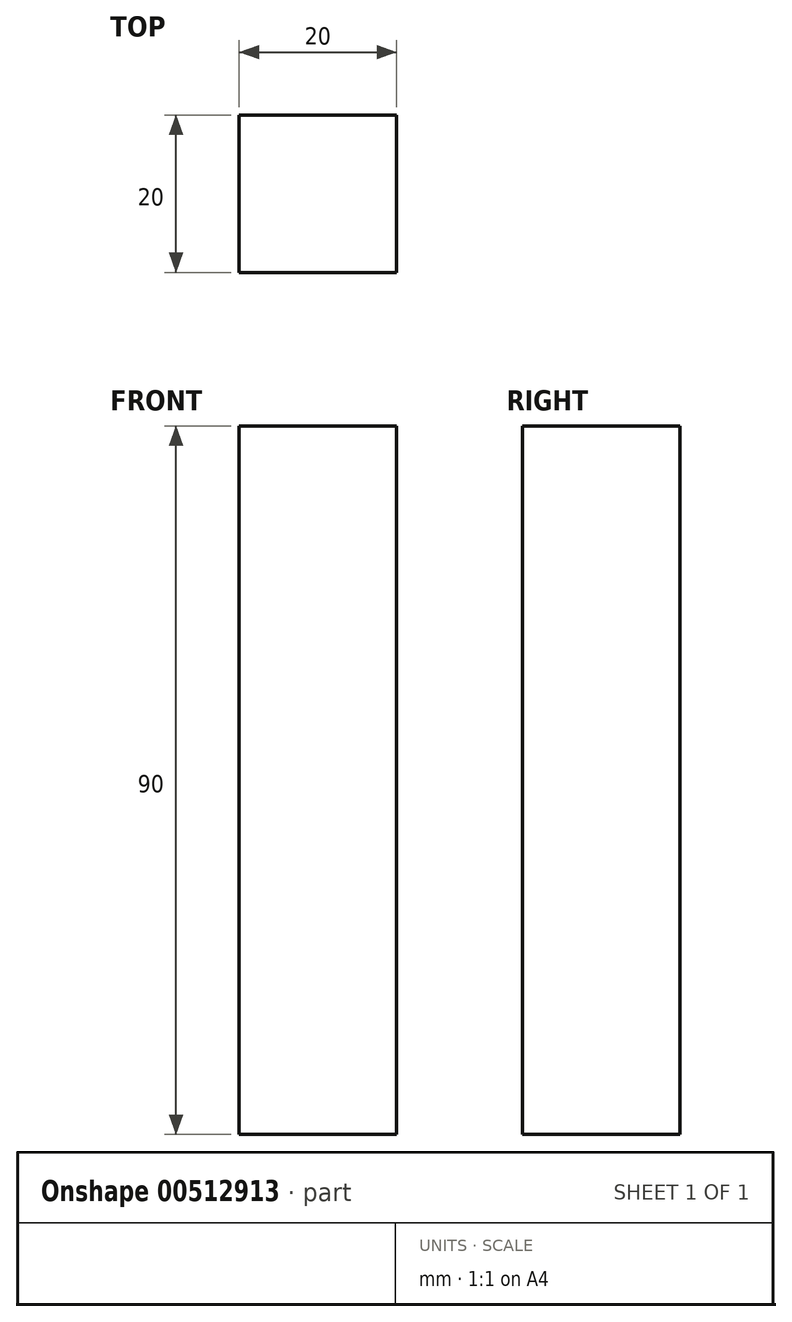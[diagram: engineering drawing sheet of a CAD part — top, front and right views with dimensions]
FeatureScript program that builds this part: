
annotation { "Feature Type Name" : "Feature", "Feature Type Description" : "" }
export const myFeature = defineFeature(function(context is Context, id is Id, definition is map)
    precondition{}
    {
        {
            var Q0;
            Q0=qCreatedBy(makeId("Top.planeOp"),FACE);
            var sketch = newSketch(context, id + "F0", { "sketchPlane" : qUnion([Q0])});
            skLineSegment(sketch, "E0.bottom", {"start": v(10, -10) * mm, "end": v(-10, -10) * mm});
            skLineSegment(sketch, "E0.top", {"start": v(10, 10) * mm, "end": v(-10, 10) * mm});
            skLineSegment(sketch, "E0.left", {"start": v(10, -10) * mm, "end": v(10, 10) * mm});
            skLineSegment(sketch, "E0.right", {"start": v(-10, -10) * mm, "end": v(-10, 10) * mm});
            skPoint(sketch, "E0.middle", {"position": v(0, 0) * mm});
            skSolve(sketch);
        }
        {
            var Q0;
            Q0=makeQuery(id+"F0.imprint","IMPRINT",FACE,{"disambiguationData":[TD([[makeQuery(id+"F0.imprint","IMPRINT",EDGE,{"derivedFrom":sQuery(id+"F0.wireOp",EDGE,"E0.bottom")}),-1.0]])]});
            extrude(context, id + "F1", {"entities" : qUnion([Q0]), "depth" : 90 * mm});
        }
    });
